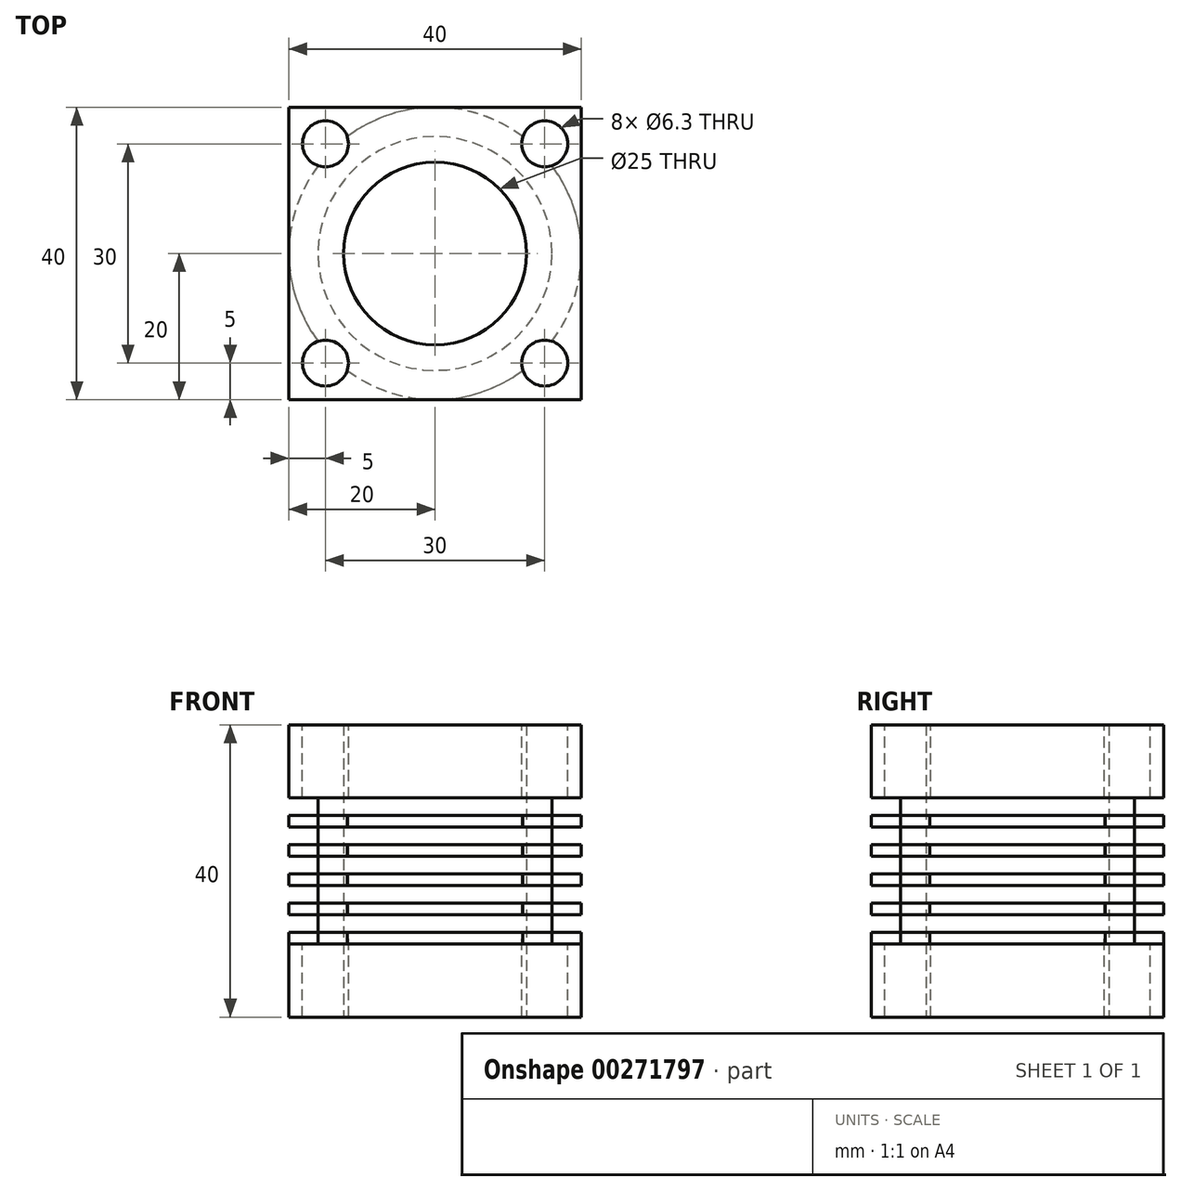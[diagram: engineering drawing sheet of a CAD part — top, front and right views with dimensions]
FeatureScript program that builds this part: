
annotation { "Feature Type Name" : "Feature", "Feature Type Description" : "" }
export const myFeature = defineFeature(function(context is Context, id is Id, definition is map)
    precondition{}
    {
        {
            var Q0;
            Q0=qCreatedBy(makeId("Top.planeOp"),FACE);
            var sketch = newSketch(context, id + "F0", { "sketchPlane" : qUnion([Q0])});
            skCircle(sketch, "E0", {"center": v(0, 0) * mm, "radius": 12.5 * mm});
            skLineSegment(sketch, "E1.bottom", {"start": v(20, -20) * mm, "end": v(-20, -20) * mm});
            skLineSegment(sketch, "E1.top", {"start": v(20, 20) * mm, "end": v(-20, 20) * mm});
            skLineSegment(sketch, "E1.left", {"start": v(20, -20) * mm, "end": v(20, 20) * mm});
            skLineSegment(sketch, "E1.right", {"start": v(-20, -20) * mm, "end": v(-20, 20) * mm});
            skSolve(sketch);
        }
        {
            var Q0;
            Q0 = qSketchRegion(id + "F0", true);
            extrude(context, id + "F1", {"entities" : qUnion([Q0]), "depth" : 10 * mm});
        }
        {
            var Q0;
            Q0=qCreatedBy(makeId("Right.planeOp"),FACE);
            var sketch = newSketch(context, id + "F2", { "sketchPlane" : qUnion([Q0])});
            skLineSegment(sketch, "E2.0", {"start": v(-20, 10) * mm, "end": v(20, 10) * mm, "construction": true});
            skLineSegment(sketch, "E3", {"start": v(0, 10) * mm, "end": v(0, 30) * mm});
            skPoint(sketch, "E3.endSnap0", {"position": v(0, 10) * mm});
            skLineSegment(sketch, "E4", {"start": v(0, 30) * mm, "end": v(20, 30) * mm});
            skLineSegment(sketch, "E5", {"start": v(0, 10) * mm, "end": v(20, 10) * mm});
            skLineSegment(sketch, "E6", {"start": v(20, 11.62) * mm, "end": v(16, 11.62) * mm});
            skLineSegment(sketch, "E7", {"start": v(20, 11.62) * mm, "end": v(20, 10) * mm});
            skLineSegment(sketch, "E8", {"start": v(16, 11.62) * mm, "end": v(16, 14) * mm});
            skLineSegment(sketch, "E9", {"start": v(16, 14) * mm, "end": v(20, 14) * mm});
            skLineSegment(sketch, "E10", {"start": v(20, 14) * mm, "end": v(20, 15.62) * mm});
            skLineSegment(sketch, "E11.1.0.0", {"start": v(20, 18) * mm, "end": v(20, 19.62) * mm});
            skLineSegment(sketch, "E11.1.0.1", {"start": v(16, 18) * mm, "end": v(20, 18) * mm});
            skLineSegment(sketch, "E11.1.0.2", {"start": v(16, 15.62) * mm, "end": v(16, 18) * mm});
            skLineSegment(sketch, "E11.1.0.3", {"start": v(20, 15.62) * mm, "end": v(16, 15.62) * mm});
            skLineSegment(sketch, "E11.2.0.0", {"start": v(20, 22) * mm, "end": v(20, 23.62) * mm});
            skLineSegment(sketch, "E11.2.0.1", {"start": v(16, 22) * mm, "end": v(20, 22) * mm});
            skLineSegment(sketch, "E11.2.0.2", {"start": v(16, 19.62) * mm, "end": v(16, 22) * mm});
            skLineSegment(sketch, "E11.2.0.3", {"start": v(20, 19.62) * mm, "end": v(16, 19.62) * mm});
            skLineSegment(sketch, "E11.3.0.0", {"start": v(20, 26) * mm, "end": v(20, 27.62) * mm});
            skLineSegment(sketch, "E11.3.0.1", {"start": v(16, 26) * mm, "end": v(20, 26) * mm});
            skLineSegment(sketch, "E11.3.0.2", {"start": v(16, 23.62) * mm, "end": v(16, 26) * mm});
            skLineSegment(sketch, "E11.3.0.3", {"start": v(20, 23.62) * mm, "end": v(16, 23.62) * mm});
            skLineSegment(sketch, "E11.4.0.2", {"start": v(16, 27.62) * mm, "end": v(16, 30) * mm});
            skLineSegment(sketch, "E11.4.0.3", {"start": v(20, 27.62) * mm, "end": v(16, 27.62) * mm});
            skLineSegment(sketch, "E11.direction1", {"start": v(16, 11.62) * mm, "end": v(16, 15.62) * mm, "construction": true});
            skSolve(sketch);
        }
        {
            var Q0;
            {var subQ1=sQuery(id+"F2.wireOp",EDGE,"E3");Q0=makeQuery(id+"F2.imprint","IMPRINT",FACE,{"disambiguationData":[TD([[makeQuery(id+"F2.imprint","IMPRINT",EDGE,{"derivedFrom":subQ1}),-1.0]])]});}
            var Q1;
            Q1=sQuery(id+"F2.wireOp",EDGE,"E3");
            revolve(context, id + "F3", {"operationType" : NewBodyOperationType.ADD, "entities" : qUnion([Q0]), "axis" : qUnion([Q1]), "revolveType" : RevolveType.FULL});
        }
        {
            var Q0;
            Q0=makeQuery(id+"F3.opRevolve","SWEPT_FACE",FACE,{"disambiguationData":[OSD([sQuery(id+"F2.wireOp",EDGE,"E4")])]});
            var sketch = newSketch(context, id + "F4", { "sketchPlane" : qUnion([Q0])});
            skLineSegment(sketch, "E12.bottom", {"start": v(20, -20) * mm, "end": v(-20, -20) * mm});
            skLineSegment(sketch, "E12.top", {"start": v(20, 20) * mm, "end": v(-20, 20) * mm});
            skLineSegment(sketch, "E12.left", {"start": v(20, -20) * mm, "end": v(20, 20) * mm});
            skLineSegment(sketch, "E12.right", {"start": v(-20, -20) * mm, "end": v(-20, 20) * mm});
            skPoint(sketch, "E12.middle", {"position": v(0, 0) * mm});
            skCircle(sketch, "E13", {"center": v(0, 0) * mm, "radius": 12.5 * mm});
            skSolve(sketch);
        }
        {
            var Q0;
            Q0=makeQuery(id+"F4.imprint","IMPRINT",FACE,{"disambiguationData":[TD([[makeQuery(id+"F4.imprint","IMPRINT",EDGE,{"derivedFrom":sQuery(id+"F4.wireOp",EDGE,"E13")}),-1.0]])]});
            var Q1;
            Q1=makeQuery(id+"F4.imprint","IMPRINT",FACE,{"disambiguationData":[TD([[makeQuery(id+"F4.imprint","IMPRINT",EDGE,{"derivedFrom":sQuery(id+"F4.wireOp",EDGE,"E12.bottom")}),-1.0]])]});
            extrude(context, id + "F5", {"entities" : qUnion([Q0, Q1]), "operationType" : NewBodyOperationType.ADD, "depth" : 10 * mm});
        }
        {
            var Q0;
            Q0=makeQuery(id+"F3.opRevolve","SWEPT_FACE",FACE,{"disambiguationData":[OSD([sQuery(id+"F2.wireOp",EDGE,"E4")])]});
            var sketch = newSketch(context, id + "F6", { "sketchPlane" : qUnion([Q0])});
            skPoint(sketch, "E14", {"position": v(0, 0) * mm});
            skSolve(sketch);
        }
        {
            var Q0;
            Q0=sQuery(id+"F6.wireOp",VERTEX,"E14");
            var Q1;
            Q1=makeQuery(id+"F1.opExtrude","SWEPT_BODY",BODY,{"disambiguationData":[OSD([sQuery(id+"F0.wireOp",EDGE,"E0"),sQuery(id+"F0.wireOp",EDGE,"E1.bottom"),sQuery(id+"F0.wireOp",EDGE,"E1.top"),sQuery(id+"F0.wireOp",EDGE,"E1.left"),sQuery(id+"F0.wireOp",EDGE,"E1.right")])]});
            hole(context, id + "F7", {"style" : HoleStyle.SIMPLE, "endStyle" : HoleEndStyle.THROUGH, "holeDiameter" : 25 * mm, "tappedDepth" : 12 * mm, "tapClearance" : 3, "locations" : qUnion([Q0]), "scope" : qUnion([Q1])});
        }
        {
            var Q0;
            Q0=makeQuery(id+"F5.opExtrude","CAP_FACE",FACE,{"disambiguationData":[OSD([sQuery(id+"F4.wireOp",EDGE,"E12.bottom"),sQuery(id+"F4.wireOp",EDGE,"E12.top"),sQuery(id+"F4.wireOp",EDGE,"E12.left"),sQuery(id+"F4.wireOp",EDGE,"E12.right"),sQuery(id+"F4.wireOp",EDGE,"E13")])],"isStart":false});
            var sketch = newSketch(context, id + "F8", { "sketchPlane" : qUnion([Q0])});
            skLineSegment(sketch, "E15.bottom", {"start": v(15, 15) * mm, "end": v(-15, 15) * mm, "construction": true});
            skLineSegment(sketch, "E15.top", {"start": v(15, -15) * mm, "end": v(-15, -15) * mm, "construction": true});
            skLineSegment(sketch, "E15.left", {"start": v(15, 15) * mm, "end": v(15, -15) * mm, "construction": true});
            skLineSegment(sketch, "E15.right", {"start": v(-15, 15) * mm, "end": v(-15, -15) * mm, "construction": true});
            skPoint(sketch, "E15.middle", {"position": v(0, 0) * mm});
            skSolve(sketch);
        }
        {
            var Q0;
            Q0=sQuery(id+"F8.wireOp",VERTEX,"E15.bottom.end");
            var Q1;
            Q1=sQuery(id+"F8.wireOp",VERTEX,"E15.bottom.start");
            var Q2;
            Q2=sQuery(id+"F8.wireOp",VERTEX,"E15.top.start");
            var Q3;
            Q3=sQuery(id+"F8.wireOp",VERTEX,"E15.top.end");
            var Q4;
            Q4=makeQuery(id+"F1.opExtrude","SWEPT_BODY",BODY,{"disambiguationData":[OSD([sQuery(id+"F0.wireOp",EDGE,"E0"),sQuery(id+"F0.wireOp",EDGE,"E1.bottom"),sQuery(id+"F0.wireOp",EDGE,"E1.top"),sQuery(id+"F0.wireOp",EDGE,"E1.left"),sQuery(id+"F0.wireOp",EDGE,"E1.right")])]});
            hole(context, id + "F9", {"style" : HoleStyle.SIMPLE, "endStyle" : HoleEndStyle.THROUGH, "standardTappedOrClearance" : lookupTablePath({ "standard" : "ISO", "fit" : "Close", "size" : "M6", "type" : "Clearance" }), "standardBlindInLast" : lookupTablePath({ "fit" : "Close", "standard" : "ISO", "size" : "M6", "type" : "Clearance" }), "holeDiameter" : 6.3 * mm, "tappedDepth" : 12 * mm, "tapClearance" : 3, "locations" : qUnion([Q0, Q1, Q2, Q3]), "scope" : qUnion([Q4])});
        }
    });
